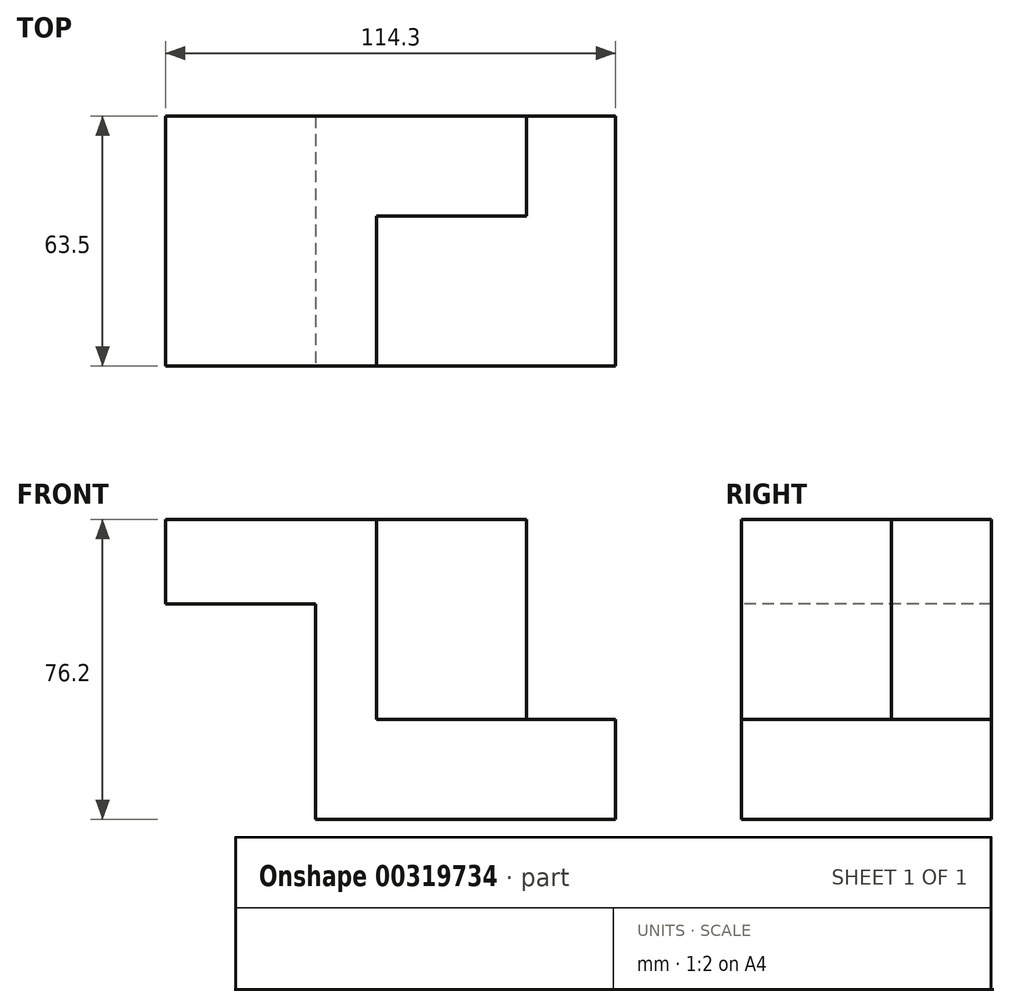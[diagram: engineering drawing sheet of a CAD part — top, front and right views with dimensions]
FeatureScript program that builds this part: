
annotation { "Feature Type Name" : "Feature", "Feature Type Description" : "" }
export const myFeature = defineFeature(function(context is Context, id is Id, definition is map)
    precondition{}
    {
        {
            var Q0;
            Q0=qCreatedBy(makeId("Top.planeOp"),FACE);
            var sketch = newSketch(context, id + "F0", { "sketchPlane" : qUnion([Q0])});
            skLineSegment(sketch, "E0", {"start": v(-29.43, 25.76) * mm, "end": v(-29.43, -37.74) * mm});
            skLineSegment(sketch, "E1", {"start": v(-29.43, -37.74) * mm, "end": v(46.77, -37.74) * mm});
            skLineSegment(sketch, "E2", {"start": v(46.77, -37.74) * mm, "end": v(46.77, 25.76) * mm});
            skLineSegment(sketch, "E3", {"start": v(46.77, 25.76) * mm, "end": v(-29.43, 25.76) * mm});
            skSolve(sketch);
        }
        {
            var Q0;
            Q0 = qSketchRegion(id + "F0", true);
            extrude(context, id + "F1", {"entities" : qUnion([Q0]), "depth" : 25.4 * mm});
        }
        {
            var Q0;
            Q0=makeQuery(id+"F1.opExtrude","CAP_FACE",FACE,{"disambiguationData":[OSD([sQuery(id+"F0.wireOp",EDGE,"E0"),sQuery(id+"F0.wireOp",EDGE,"E1"),sQuery(id+"F0.wireOp",EDGE,"E2"),sQuery(id+"F0.wireOp",EDGE,"E3")])],"isStart":false});
            var sketch = newSketch(context, id + "F2", { "sketchPlane" : qUnion([Q0])});
            skLineSegment(sketch, "E4", {"start": v(-14, -37.74) * mm, "end": v(-14, 0.36) * mm});
            skLineSegment(sketch, "E5", {"start": v(-14, 0.36) * mm, "end": v(24.1, 0.36) * mm});
            skLineSegment(sketch, "E6", {"start": v(24.1, 0.36) * mm, "end": v(24.1, 25.76) * mm});
            skSolve(sketch);
        }
        {
            var Q0;
            {var subQ2=sQuery(id+"F2.wireOp",EDGE,"E4");Q0=makeQuery(id+"F2.imprint","IMPRINT",FACE,{"disambiguationData":[TD([[makeQuery(id+"F2.imprint","IMPRINT",EDGE,{"derivedFrom":subQ2}),1.0]])]});}
            extrude(context, id + "F3", {"entities" : qUnion([Q0]), "operationType" : NewBodyOperationType.ADD, "depth" : 50.8 * mm});
        }
        {
            var Q0;
            {var subQ0=sQuery(id+"F0.wireOp",EDGE,"E0");Q0=makeQuery(id+"F3.boolean.opBoolean","MERGE",FACE,{"derivedFrom":[makeQuery(id+"F1.opExtrude","SWEPT_FACE",FACE,{"disambiguationData":[OSD([subQ0])]}),makeQuery(id+"F3.opExtrude","SWEPT_FACE",FACE,{"disambiguationData":[OSD([subQ0])]})]});}
            var sketch = newSketch(context, id + "F4", { "sketchPlane" : qUnion([Q0])});
            skLineSegment(sketch, "E7", {"start": v(-25.76, 76.2) * mm, "end": v(-25.76, 54.73) * mm});
            skLineSegment(sketch, "E8", {"start": v(-25.76, 54.73) * mm, "end": v(37.74, 54.73) * mm});
            skLineSegment(sketch, "E9", {"start": v(37.74, 54.73) * mm, "end": v(37.74, 76.2) * mm});
            skLineSegment(sketch, "E10", {"start": v(37.74, 76.2) * mm, "end": v(-25.76, 76.2) * mm});
            skSolve(sketch);
        }
        {
            var Q0;
            Q0=makeQuery(id+"F4.imprint","IMPRINT",FACE,{"disambiguationData":[TD([[makeQuery(id+"F4.imprint","IMPRINT",EDGE,{"derivedFrom":sQuery(id+"F4.wireOp",EDGE,"E7")}),1.0]])]});
            extrude(context, id + "F5", {"entities" : qUnion([Q0]), "operationType" : NewBodyOperationType.ADD, "depth" : 38.1 * mm});
        }
    });
